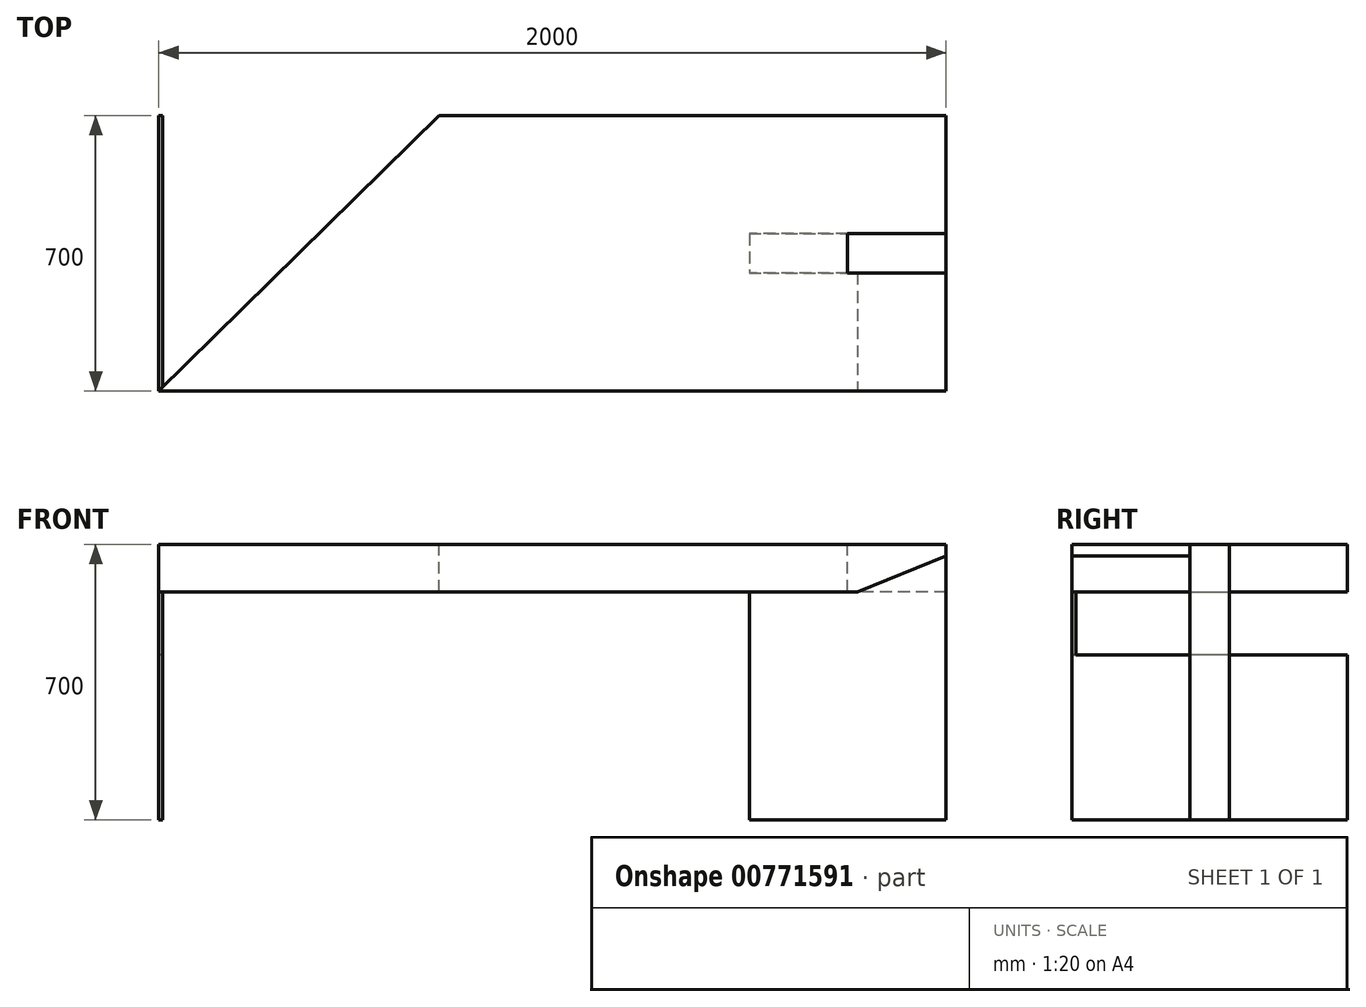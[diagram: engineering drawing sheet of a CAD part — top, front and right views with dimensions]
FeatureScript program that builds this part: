
annotation { "Feature Type Name" : "Feature", "Feature Type Description" : "" }
export const myFeature = defineFeature(function(context is Context, id is Id, definition is map)
    precondition{}
    {
        {
            var Q0;
            Q0=qCreatedBy(makeId("Front.planeOp"),FACE);
            var sketch = newSketch(context, id + "F0", { "sketchPlane" : qUnion([Q0])});
            skLineSegment(sketch, "E0.bottom", {"start": v(-232.73, -363.19) * mm, "end": v(267.27, -363.19) * mm});
            skLineSegment(sketch, "E0.top", {"start": v(-232.73, 336.81) * mm, "end": v(267.27, 336.81) * mm});
            skLineSegment(sketch, "E0.left", {"start": v(-232.73, -363.19) * mm, "end": v(-232.73, 336.81) * mm});
            skLineSegment(sketch, "E0.right", {"start": v(267.27, -363.19) * mm, "end": v(267.27, 336.81) * mm});
            skSolve(sketch);
        }
        {
            var Q0;
            Q0=makeQuery(id+"F0.imprint","IMPRINT",FACE,{"disambiguationData":[TD([[makeQuery(id+"F0.imprint","IMPRINT",EDGE,{"derivedFrom":sQuery(id+"F0.wireOp",EDGE,"E0.bottom")}),1.0]])]});
            extrude(context, id + "F1", {"entities" : qUnion([Q0]), "depth" : 100 * mm, "offsetDistance" : 25 * mm});
        }
        {
            var Q0;
            Q0=makeQuery(id+"F1.opExtrude","CAP_FACE",FACE,{"disambiguationData":[OSD([sQuery(id+"F0.wireOp",EDGE,"E0.bottom"),sQuery(id+"F0.wireOp",EDGE,"E0.top"),sQuery(id+"F0.wireOp",EDGE,"E0.left"),sQuery(id+"F0.wireOp",EDGE,"E0.right")])],"isStart":false});
            var sketch = newSketch(context, id + "F2", { "sketchPlane" : qUnion([Q0])});
            skLineSegment(sketch, "E1.bottom", {"start": v(17.27, 336.81) * mm, "end": v(-232.73, 336.81) * mm});
            skLineSegment(sketch, "E1.top", {"start": v(17.27, 216.81) * mm, "end": v(-232.73, 216.81) * mm});
            skLineSegment(sketch, "E1.left", {"start": v(17.27, 336.81) * mm, "end": v(17.27, 216.81) * mm});
            skLineSegment(sketch, "E1.right", {"start": v(-232.73, 336.81) * mm, "end": v(-232.73, 216.81) * mm});
            skSolve(sketch);
        }
        {
            var Q0;
            Q0=makeQuery(id+"F2.imprint","IMPRINT",FACE,{"disambiguationData":[TD([[makeQuery(id+"F2.imprint","IMPRINT",EDGE,{"derivedFrom":sQuery(id+"F2.wireOp",EDGE,"E1.bottom")}),-1.0]])]});
            extrude(context, id + "F3", {"entities" : qUnion([Q0]), "operationType" : NewBodyOperationType.REMOVE, "oppositeDirection" : true, "depth" : 231 * mm, "offsetDistance" : 25 * mm});
        }
        {
            var Q0;
            Q0=makeQuery(id+"F1.opExtrude","SWEPT_FACE",FACE,{"disambiguationData":[OSD([sQuery(id+"F0.wireOp",EDGE,"E0.top")])]});
            var sketch = newSketch(context, id + "F4", { "sketchPlane" : qUnion([Q0])});
            skLineSegment(sketch, "E2", {"start": v(267.27, -50) * mm, "end": v(267.27, 300) * mm});
            skLineSegment(sketch, "E3", {"start": v(267.27, -50) * mm, "end": v(267.27, -400) * mm});
            skLineSegment(sketch, "E4", {"start": v(267.27, 300) * mm, "end": v(-1732.73, 300) * mm});
            skLineSegment(sketch, "E5", {"start": v(-1732.73, 300) * mm, "end": v(-1732.73, -400) * mm});
            skLineSegment(sketch, "E6", {"start": v(-1732.73, -400) * mm, "end": v(267.27, -400) * mm});
            skSolve(sketch);
        }
        {
            var Q0;
            {var subQ0=sQuery(id+"F4.wireOp",EDGE,"E4");Q0=makeQuery(id+"F4.imprint","IMPRINT",FACE,{"disambiguationData":[TD([[makeQuery(id+"F4.imprint","IMPRINT",EDGE,{"derivedFrom":subQ0}),1.0]])]});}
            var Q1;
            Q1=makeQuery(id+"F3.boolean.opBoolean","COPY",FACE,{"derivedFrom":makeQuery(id+"F3.opExtrude","SWEPT_FACE",FACE,{"disambiguationData":[OSD([sQuery(id+"F2.wireOp",EDGE,"E1.top")])]})});
            extrude(context, id + "F5", {"entities" : qUnion([Q0]), "endBound" : BoundingType.UP_TO_SURFACE, "oppositeDirection" : true, "depth" : 70 * mm, "endBoundEntityFace" : qUnion([Q1]), "offsetDistance" : 25 * mm});
        }
        {
            var Q0;
            Q0=makeQuery(id+"F5.opExtrude","CAP_FACE",FACE,{"disambiguationData":[OSD([sQuery(id+"F0.wireOp",EDGE,"E0.top"),sQuery(id+"F2.wireOp",EDGE,"E1.bottom"),sQuery(id+"F2.wireOp",EDGE,"E1.left"),sQuery(id+"F4.wireOp",EDGE,"E2"),sQuery(id+"F4.wireOp",EDGE,"E3"),sQuery(id+"F4.wireOp",EDGE,"E4"),sQuery(id+"F4.wireOp",EDGE,"E5"),sQuery(id+"F4.wireOp",EDGE,"E6")])],"isStart":false});
            var sketch = newSketch(context, id + "F6", { "sketchPlane" : qUnion([Q0])});
            skLineSegment(sketch, "E7.bottom", {"start": v(-1732.73, 400) * mm, "end": v(-1722.73, 400) * mm});
            skLineSegment(sketch, "E7.top", {"start": v(-1732.73, -300) * mm, "end": v(-1722.73, -300) * mm});
            skLineSegment(sketch, "E7.left", {"start": v(-1732.73, 400) * mm, "end": v(-1732.73, -300) * mm});
            skLineSegment(sketch, "E7.right", {"start": v(-1722.73, 400) * mm, "end": v(-1722.73, -300) * mm});
            skSolve(sketch);
        }
        {
            var Q0;
            Q0 = qSketchRegion(id + "F6", true);
            var Q1;
            Q1=makeQuery(id+"F1.opExtrude","SWEPT_FACE",FACE,{"disambiguationData":[OSD([sQuery(id+"F0.wireOp",EDGE,"E0.bottom")])]});
            extrude(context, id + "F7", {"entities" : qUnion([Q0]), "endBound" : BoundingType.UP_TO_SURFACE, "depth" : 610 * mm, "endBoundEntityFace" : qUnion([Q1]), "offsetDistance" : 25 * mm});
        }
        {
            var Q0;
            Q0=makeQuery(id+"F5.opExtrude","SWEPT_FACE",FACE,{"disambiguationData":[OSD([sQuery(id+"F4.wireOp",EDGE,"E6")])]});
            var sketch = newSketch(context, id + "F8", { "sketchPlane" : qUnion([Q0])});
            skLineSegment(sketch, "E8", {"start": v(42.14, 216.81) * mm, "end": v(267.27, 307.25) * mm});
            skSolve(sketch);
        }
        {
            var Q0;
            Q0 = qSketchRegion(id + "F8", true);
            var Q1;
            {var subQ0=sQuery(id+"F8.wireOp",EDGE,"E8");Q1=makeQuery(id+"F8.imprint","IMPRINT",FACE,{"disambiguationData":[TD([[makeQuery(id+"F8.imprint","IMPRINT",EDGE,{"derivedFrom":subQ0}),-1.0]])]});}
            var Q2;
            Q2=makeQuery(id+"F1.opExtrude","CAP_FACE",FACE,{"disambiguationData":[OSD([sQuery(id+"F0.wireOp",EDGE,"E0.bottom"),sQuery(id+"F0.wireOp",EDGE,"E0.top"),sQuery(id+"F0.wireOp",EDGE,"E0.left"),sQuery(id+"F0.wireOp",EDGE,"E0.right")])],"isStart":false});
            extrude(context, id + "F9", {"entities" : qUnion([Q0, Q1]), "operationType" : NewBodyOperationType.REMOVE, "endBound" : BoundingType.UP_TO_SURFACE, "oppositeDirection" : true, "depth" : 940 * mm, "endBoundEntityFace" : qUnion([Q2]), "offsetDistance" : 25 * mm});
        }
        {
            var Q0;
            Q0=makeQuery(id+"F5.opExtrude","CAP_FACE",FACE,{"disambiguationData":[OSD([sQuery(id+"F0.wireOp",EDGE,"E0.top"),sQuery(id+"F2.wireOp",EDGE,"E1.bottom"),sQuery(id+"F2.wireOp",EDGE,"E1.left"),sQuery(id+"F4.wireOp",EDGE,"E2"),sQuery(id+"F4.wireOp",EDGE,"E3"),sQuery(id+"F4.wireOp",EDGE,"E4"),sQuery(id+"F4.wireOp",EDGE,"E5"),sQuery(id+"F4.wireOp",EDGE,"E6")])],"isStart":true});
            var sketch = newSketch(context, id + "F10", { "sketchPlane" : qUnion([Q0])});
            skLineSegment(sketch, "E9", {"start": v(-1732.73, -400) * mm, "end": v(-1021.25, 300) * mm});
            skSolve(sketch);
        }
        {
            var Q0;
            {var subQ0=sQuery(id+"F10.wireOp",EDGE,"E9");Q0=makeQuery(id+"F10.imprint","IMPRINT",FACE,{"disambiguationData":[TD([[makeQuery(id+"F10.imprint","IMPRINT",EDGE,{"derivedFrom":subQ0}),1.0]])]});}
            extrude(context, id + "F11", {"entities" : qUnion([Q0]), "operationType" : NewBodyOperationType.REMOVE, "oppositeDirection" : true, "depth" : 280 * mm, "offsetDistance" : 25 * mm});
        }
    });
